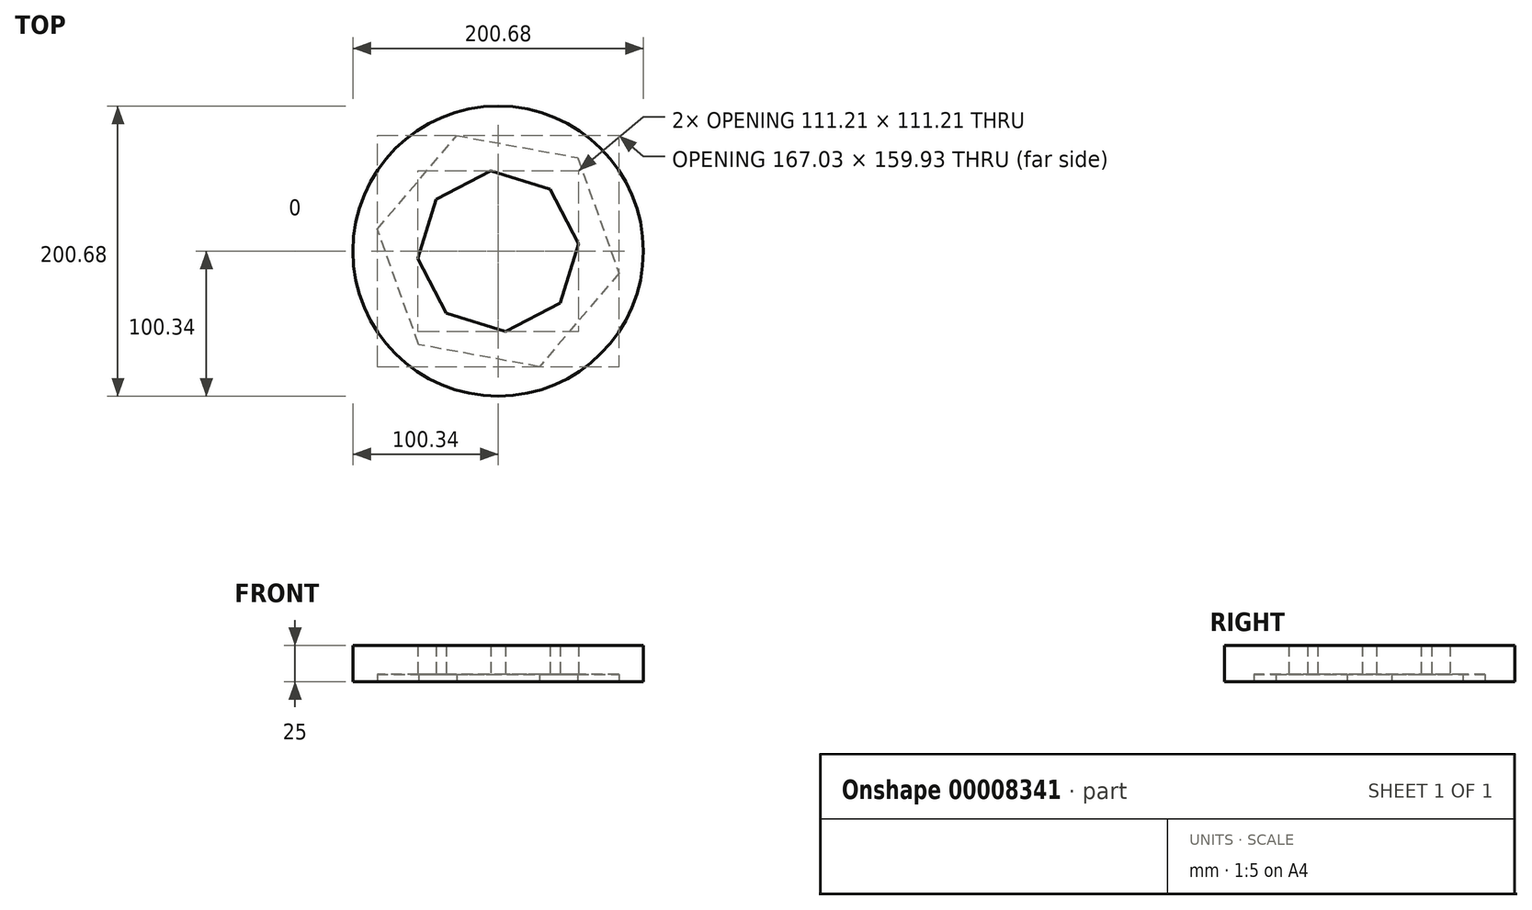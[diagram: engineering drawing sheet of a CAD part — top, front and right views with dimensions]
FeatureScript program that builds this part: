
annotation { "Feature Type Name" : "Feature", "Feature Type Description" : "" }
export const myFeature = defineFeature(function(context is Context, id is Id, definition is map)
    precondition{}
    {
        {
            var Q0;
            Q0=qCreatedBy(makeId("Top.planeOp"),FACE);
            var sketch = newSketch(context, id + "F0", { "sketchPlane" : qUnion([Q0])});
            skCircle(sketch, "E0", {"center": v(0, 0) * mm, "radius": 100.34 * mm});
            skSolve(sketch);
        }
        {
            var Q0;
            Q0=makeQuery(id+"F0.imprint","IMPRINT",FACE,{"disambiguationData":[TD([[makeQuery(id+"F0.imprint","IMPRINT",EDGE,{"derivedFrom":sQuery(id+"F0.wireOp",EDGE,"E0")}),1.0]])]});
            var sketch = newSketch(context, id + "F1", { "sketchPlane" : qUnion([Q0])});
            skCircle(sketch, "E1.cCircle", {"center": v(0, 0) * mm, "radius": 51.58 * mm, "construction": true});
            skLineSegment(sketch, "E1.0", {"start": v(-35.78, -42.85) * mm, "end": v(-55.6, -5) * mm});
            skLineSegment(sketch, "E1.1", {"start": v(-55.6, -5) * mm, "end": v(-42.85, 35.78) * mm});
            skLineSegment(sketch, "E1.2", {"start": v(-42.85, 35.78) * mm, "end": v(-5, 55.6) * mm});
            skLineSegment(sketch, "E1.3", {"start": v(-5, 55.6) * mm, "end": v(35.78, 42.85) * mm});
            skLineSegment(sketch, "E1.4", {"start": v(35.78, 42.85) * mm, "end": v(55.6, 5) * mm});
            skLineSegment(sketch, "E1.5", {"start": v(55.6, 5) * mm, "end": v(42.85, -35.78) * mm});
            skLineSegment(sketch, "E1.6", {"start": v(42.85, -35.78) * mm, "end": v(5, -55.6) * mm});
            skLineSegment(sketch, "E1.7", {"start": v(5, -55.6) * mm, "end": v(-35.78, -42.85) * mm});
            skPoint(sketch, "E1.0.midPoint", {"position": v(-45.7, -23.93) * mm});
            skSolve(sketch);
        }
        {
            var Q0;
            Q0=makeQuery(id+"F1.imprint","IMPRINT",FACE,{"disambiguationData":[TD([[makeQuery(id+"F1.imprint","IMPRINT",EDGE,{"derivedFrom":sQuery(id+"F1.wireOp",EDGE,"E1.0")}),1.0]])]});
            extrude(context, id + "F2", {"entities" : qUnion([Q0]), "depth" : 25 * mm});
        }
        {
            var Q0;
            Q0=makeQuery(id+"F0.imprint","IMPRINT",FACE,{"disambiguationData":[TD([[makeQuery(id+"F0.imprint","IMPRINT",EDGE,{"derivedFrom":sQuery(id+"F0.wireOp",EDGE,"E0")}),1.0]])]});
            var sketch = newSketch(context, id + "F3", { "sketchPlane" : qUnion([Q0])});
            skCircle(sketch, "E2.cCircle", {"center": v(0, 0) * mm, "radius": 73.53 * mm, "construction": true});
            skLineSegment(sketch, "E2.0", {"start": v(55, 64.69) * mm, "end": v(83.52, -15.28) * mm});
            skLineSegment(sketch, "E2.1", {"start": v(83.52, -15.28) * mm, "end": v(28.53, -79.97) * mm});
            skLineSegment(sketch, "E2.2", {"start": v(28.53, -79.97) * mm, "end": v(-55, -64.69) * mm});
            skLineSegment(sketch, "E2.3", {"start": v(-55, -64.69) * mm, "end": v(-83.52, 15.28) * mm});
            skLineSegment(sketch, "E2.4", {"start": v(-83.52, 15.28) * mm, "end": v(-28.53, 79.97) * mm});
            skLineSegment(sketch, "E2.5", {"start": v(-28.53, 79.97) * mm, "end": v(55, 64.69) * mm});
            skPoint(sketch, "E2.0.midPoint", {"position": v(69.25, 24.7) * mm});
            skSolve(sketch);
        }
        {
            var Q0;
            Q0=makeQuery(id+"F3.imprint","IMPRINT",FACE,{"disambiguationData":[TD([[makeQuery(id+"F3.imprint","IMPRINT",EDGE,{"derivedFrom":sQuery(id+"F3.wireOp",EDGE,"E2.0")}),-1.0]])]});
            extrude(context, id + "F4", {"entities" : qUnion([Q0]), "operationType" : NewBodyOperationType.REMOVE, "depth" : 5 * mm});
        }
    });
